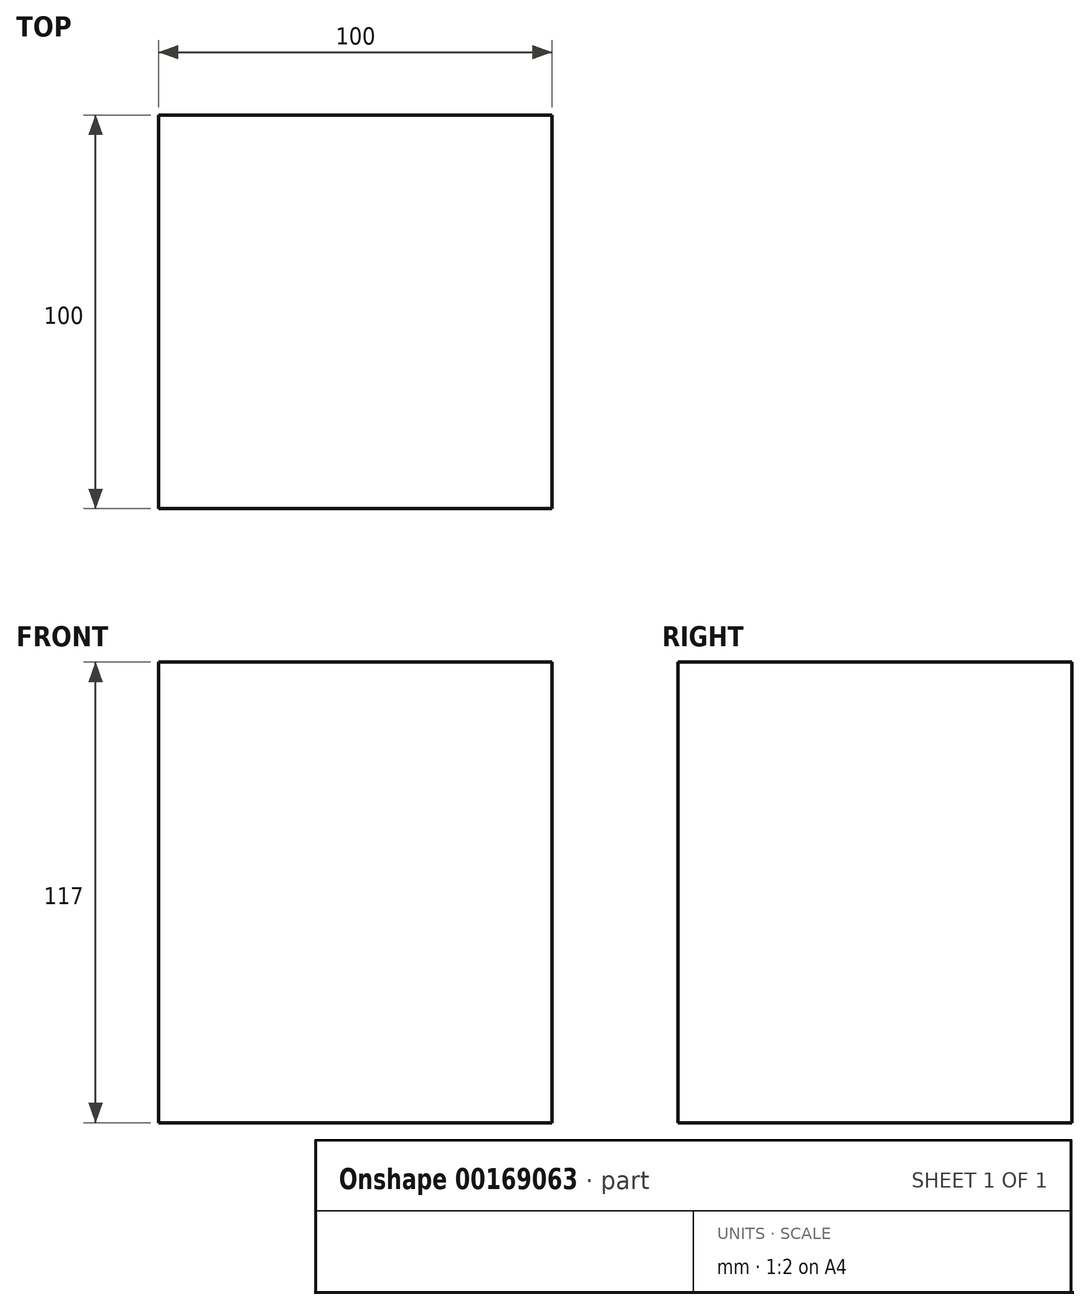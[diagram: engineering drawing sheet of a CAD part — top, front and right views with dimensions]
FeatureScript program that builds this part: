
annotation { "Feature Type Name" : "Feature", "Feature Type Description" : "" }
export const myFeature = defineFeature(function(context is Context, id is Id, definition is map)
    precondition{}
    {
        {
            var Q0;
            Q0=qCreatedBy(makeId("Top.planeOp"),FACE);
            var sketch = newSketch(context, id + "F0", { "sketchPlane" : qUnion([Q0])});
            skLineSegment(sketch, "E0.bottom", {"start": v(50, 50) * mm, "end": v(-50, 50) * mm});
            skLineSegment(sketch, "E0.top", {"start": v(50, -50) * mm, "end": v(-50, -50) * mm});
            skLineSegment(sketch, "E0.left", {"start": v(50, 50) * mm, "end": v(50, -50) * mm});
            skLineSegment(sketch, "E0.right", {"start": v(-50, 50) * mm, "end": v(-50, -50) * mm});
            skPoint(sketch, "E0.middle", {"position": v(0, 0) * mm});
            skSolve(sketch);
        }
        {
            var Q0;
            Q0 = qSketchRegion(id + "F0", true);
            extrude(context, id + "F1", {"entities" : qUnion([Q0]), "depth" : 117 * mm});
        }
    });
